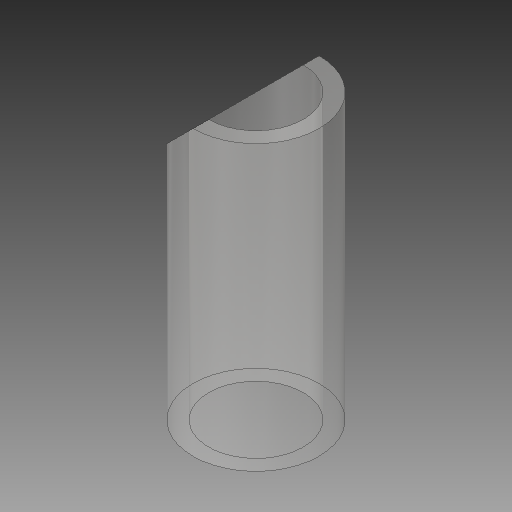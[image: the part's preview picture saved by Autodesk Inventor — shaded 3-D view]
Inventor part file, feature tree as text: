
AUTODESK INVENTOR PART (.ipt)
format: ipt  version: 2019 (Build 230136000, 136)  size: 112,640 bytes
history: native  units: mm
features: extrude x2, sketch x2
ambient origin geometry x8: Origin, YZ Plane, XZ Plane, XY Plane, X Axis, Y Axis, Z Axis, Center Point
bodies: Solid1 (feature_tree)
feature tree (4):
  extrude  "Extrusion1"  Depth=40.0mm
  extrude  "Extrusion2"  Depth=20.0mm TaperAngle=0.0deg
  sketch  "Sketch1"  dims[d0=30.0mm d1=40.0mm]
  sketch  "Sketch2"  dims[d2=90.0mm d3=0.0mm d5=115.0mm d6=0.0mm d7=20.0mm d9=45.0deg]
